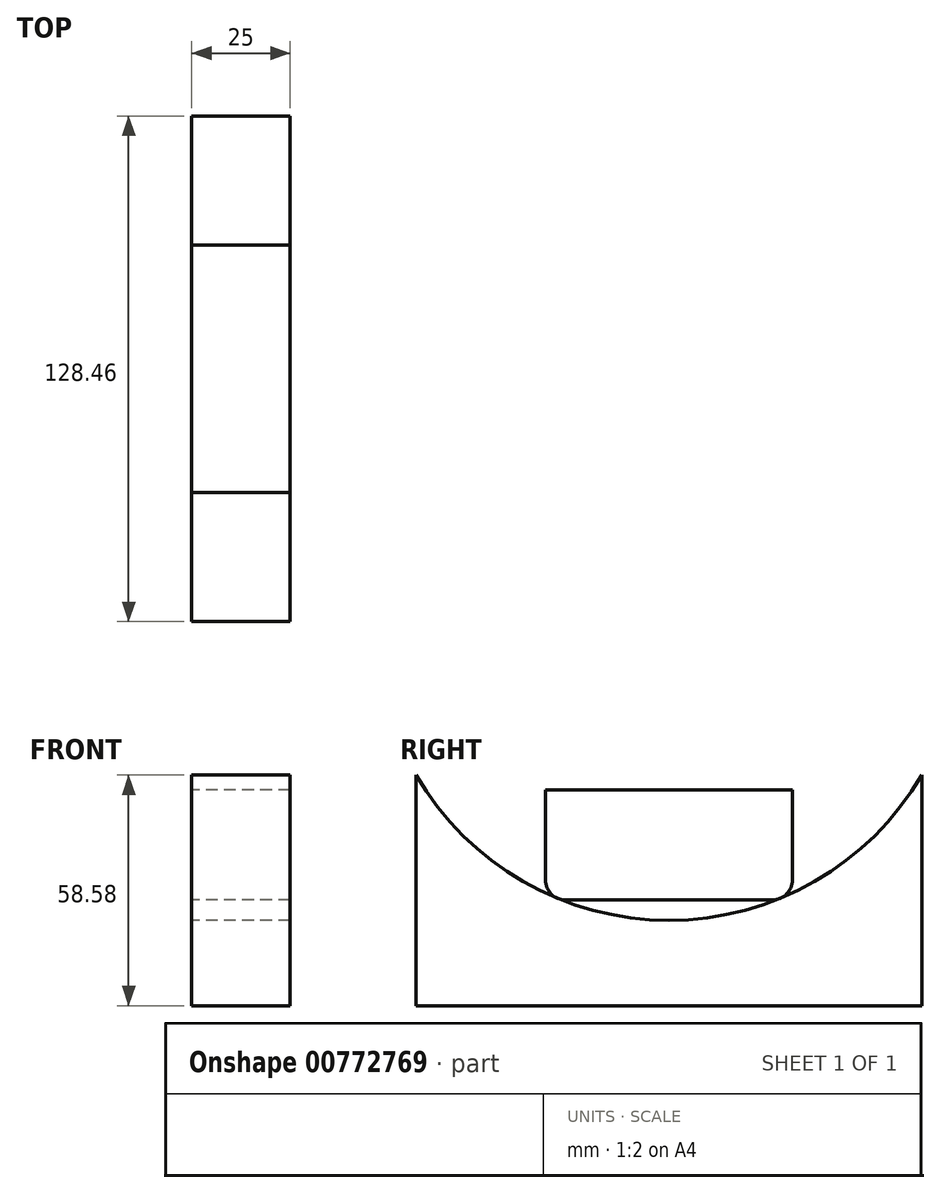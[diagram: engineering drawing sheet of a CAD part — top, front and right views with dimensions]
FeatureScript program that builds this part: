
annotation { "Feature Type Name" : "Feature", "Feature Type Description" : "" }
export const myFeature = defineFeature(function(context is Context, id is Id, definition is map)
    precondition{}
    {
        {
            var Q0;
            Q0=qCreatedBy(makeId("Right.planeOp"),FACE);
            var sketch = newSketch(context, id + "F0", { "sketchPlane" : qUnion([Q0])});
            skArc(sketch, "E0", {"start": v(-64.23, 0) * mm, "mid": v(0, -36.9) * mm, "end": v(64.23, 0) * mm});
            skLineSegment(sketch, "E1", {"start": v(-64.23, 0) * mm, "end": v(-64.23, -58.58) * mm});
            skLineSegment(sketch, "E2", {"start": v(64.23, -58.58) * mm, "end": v(64.23, 0) * mm});
            skLineSegment(sketch, "E3", {"start": v(-64.23, -58.58) * mm, "end": v(64.23, -58.58) * mm});
            skSolve(sketch);
        }
        {
            var Q0;
            Q0=makeQuery(id+"F0.imprint","IMPRINT",FACE,{"disambiguationData":[TD([[makeQuery(id+"F0.imprint","IMPRINT",EDGE,{"derivedFrom":sQuery(id+"F0.wireOp",EDGE,"E0")}),-1.0]])]});
            extrude(context, id + "F1", {"entities" : qUnion([Q0]), "depth" : 25 * mm, "offsetDistance" : 25 * mm});
        }
        {
            var Q0;
            Q0=qCreatedBy(makeId("Right.planeOp"),FACE);
            var sketch = newSketch(context, id + "F2", { "sketchPlane" : qUnion([Q0])});
            skLineSegment(sketch, "E4.bottom", {"start": v(-31.37, -3.76) * mm, "end": v(31.37, -3.76) * mm});
            skLineSegment(sketch, "E4.top", {"start": v(-26.37, -31.68) * mm, "end": v(26.37, -31.68) * mm});
            skLineSegment(sketch, "E4.left", {"start": v(-31.37, -3.76) * mm, "end": v(-31.37, -26.68) * mm});
            skLineSegment(sketch, "E4.right", {"start": v(31.37, -3.76) * mm, "end": v(31.37, -26.68) * mm});
            skPoint(sketch, "E5.visualSharp", {"position": v(-31.37, -31.68) * mm});
            skArc(sketch, "E5.filletArc", {"start": v(-31.37, -26.68) * mm, "mid": v(-29.9, -30.22) * mm, "end": v(-26.37, -31.68) * mm});
            skPoint(sketch, "E6.visualSharp", {"position": v(31.37, -31.68) * mm});
            skArc(sketch, "E6.filletArc", {"start": v(26.37, -31.68) * mm, "mid": v(29.9, -30.22) * mm, "end": v(31.37, -26.68) * mm});
            skSolve(sketch);
        }
        {
            var Q0;
            Q0=makeQuery(id+"F2.imprint","IMPRINT",FACE,{"disambiguationData":[TD([[makeQuery(id+"F2.imprint","IMPRINT",EDGE,{"derivedFrom":sQuery(id+"F2.wireOp",EDGE,"E4.bottom")}),-1.0]])]});
            extrude(context, id + "F3", {"entities" : qUnion([Q0]), "depth" : 25 * mm, "offsetDistance" : 25 * mm});
        }
    });
